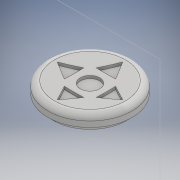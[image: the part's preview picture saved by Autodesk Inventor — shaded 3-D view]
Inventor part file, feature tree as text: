
AUTODESK INVENTOR PART (.ipt)
format: ipt  version: 2018 (Build 220112000, 112)  size: 183,808 bytes
history: native  units: mm
features: sketch x4, extrude x3, revolve x1, pattern_circular x1, chamfer x1
ambient origin geometry x8: Origin, YZ Plane, XZ Plane, XY Plane, X Axis, Y Axis, Z Axis, Center Point
bodies: Solid1 (feature_tree)
feature tree (10):
  sketch  "Sketch2"  dims[d0=15.0mm d3=90.0deg]
  revolve  "Revolution1"  Angle=90.0deg
  extrude  "Extrusion1"  Depth=2.0mm
  sketch  "Sketch5"  dims[d9=3.0mm d10=1.0mm d11=0.5mm d12=60.0deg d13=3.0mm d14=0.5mm d15=0.0mm d16=40.0mm d17=360.0deg d19=0.5mm d20=0.0mm d21=1.0mm d22=1.0mm d23=45.0deg]
  extrude  "Extrusion2"  Depth=1.5mm
  pattern_circular  "Circular Pattern1"  [2 undecoded]
  extrude  "Extrusion3"  Depth=0.5mm
  chamfer  "Chamfer1"  Angle=60.0deg  [1 undecoded]
  sketch  "Sketch3"  dims[d4=2.0mm d5=2.0mm]
  sketch  "Sketch4"  dims[d6=1.5mm d7=0.0mm d8=2.5mm]
note: 3 required parameter values undecoded (feature->parameter linkage not recoverable at this tier; creation-order binding heuristic only, values carry confidence <= 0.55)
